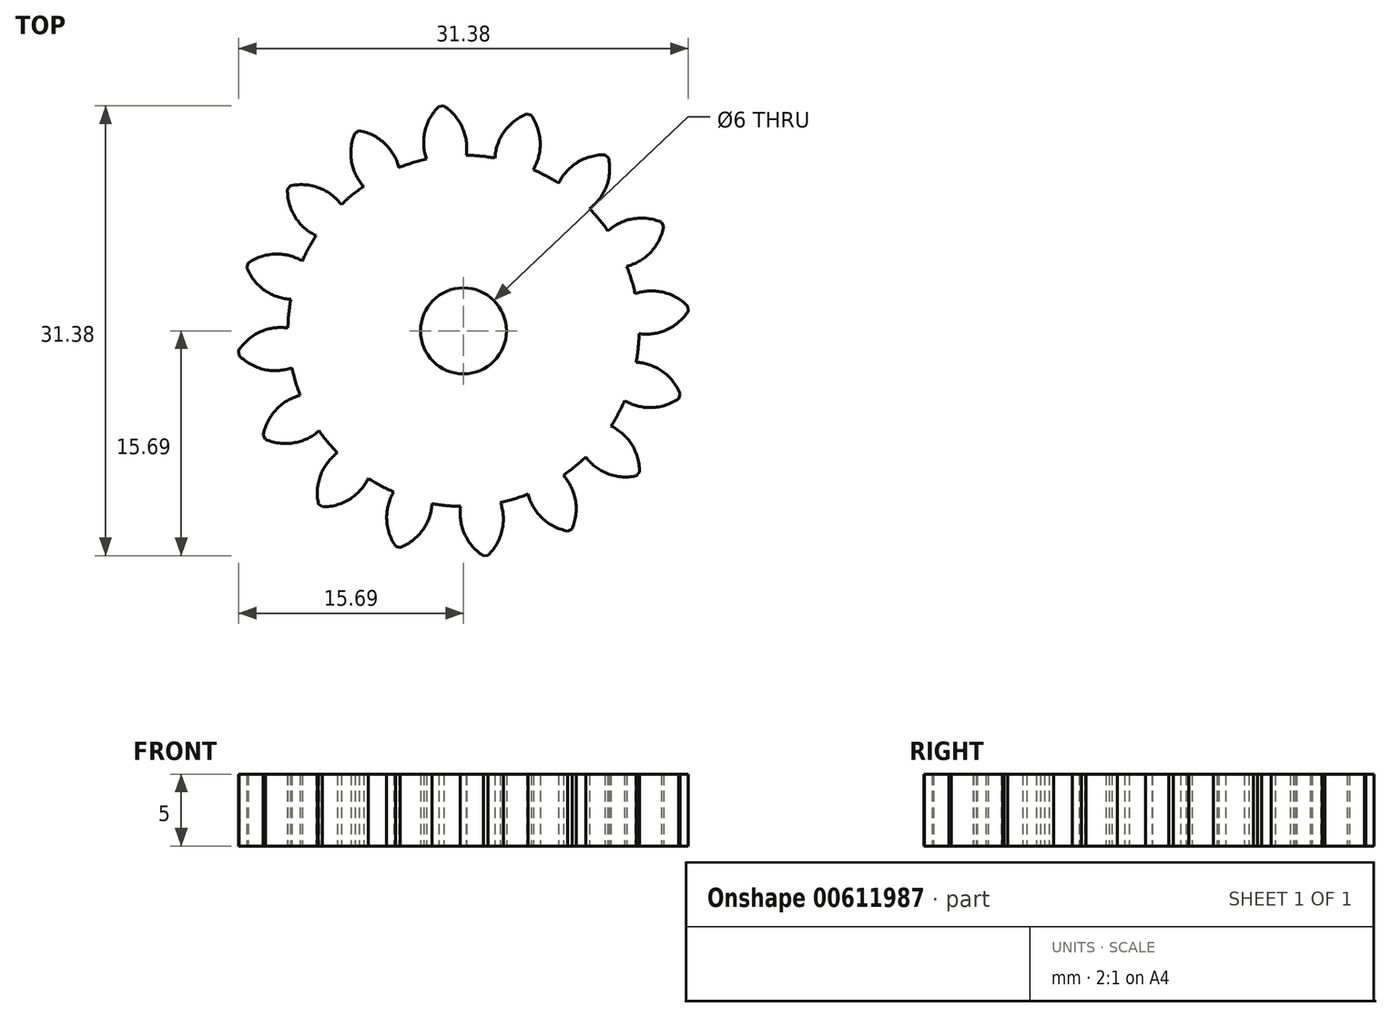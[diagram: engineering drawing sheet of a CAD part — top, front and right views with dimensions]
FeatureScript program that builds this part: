
annotation { "Feature Type Name" : "Feature", "Feature Type Description" : "" }
export const myFeature = defineFeature(function(context is Context, id is Id, definition is map)
    precondition{}
    {
        {
            var Q0;
            Q0=qCreatedBy(makeId("Top.planeOp"),FACE);
            var sketch = newSketch(context, id + "F0", { "sketchPlane" : qUnion([Q0])});
            skCircle(sketch, "E0", {"center": v(0, 0) * mm, "radius": 12.25 * mm});
            skCircle(sketch, "E1", {"center": v(0, 0) * mm, "radius": 14 * mm, "construction": true});
            skCircle(sketch, "E2", {"center": v(0, 0) * mm, "radius": 15.75 * mm, "construction": true});
            skLineSegment(sketch, "E3", {"start": v(0, 0) * mm, "end": v(0, 25.23) * mm, "construction": true});
            skLineSegment(sketch, "E4", {"start": v(0, 0) * mm, "end": v(-2.42, 24.56) * mm, "construction": true});
            skLineSegment(sketch, "E5", {"start": v(0, 14) * mm, "end": v(-23.42, 14) * mm, "construction": true});
            skLineSegment(sketch, "E6", {"start": v(0, 14) * mm, "end": v(-21.75, 6.08) * mm, "construction": true});
            skCircle(sketch, "E7", {"center": v(0, 14) * mm, "radius": 3.5 * mm, "construction": true});
            skCircle(sketch, "E8", {"center": v(0, 0) * mm, "radius": 13.16 * mm, "construction": true});
            skCircle(sketch, "E9", {"center": v(-3.27, 12.74) * mm, "radius": 3.5 * mm, "construction": true});
            skArc(sketch, "E10", {"start": v(0, 14) * mm, "mid": v(-0.56, 14.95) * mm, "end": v(-1.38, 15.69) * mm});
            skArc(sketch, "E11", {"start": v(0.2, 12.25) * mm, "mid": v(0.2, 13.14) * mm, "end": v(0, 14) * mm});
            skArc(sketch, "E12.MirrorCS", {"start": v(-2.73, 13.73) * mm, "mid": v(-2.37, 14.77) * mm, "end": v(-1.71, 15.66) * mm});
            skArc(sketch, "E13.MirrorCS", {"start": v(-2.58, 11.97) * mm, "mid": v(-2.77, 12.84) * mm, "end": v(-2.73, 13.73) * mm});
            skLineSegment(sketch, "E14", {"start": v(-1.71, 15.66) * mm, "end": v(-1.38, 15.69) * mm});
            skSolve(sketch);
        }
        {
            var Q0;
            {var subQ0=sQuery(id+"F0.wireOp",EDGE,"E0");var subQ1=makeQuery(id+"F0.imprint","INTERSECT",VERTEX,{"derivedFrom":[subQ0,sQuery(id+"F0.wireOp",EDGE,"E11")]});Q0=makeQuery(id+"F0.imprint","IMPRINT",FACE,{"disambiguationData":[TD([[makeQuery(id+"F0.imprint","IMPRINT",EDGE,{"disambiguationData":[TD([[subQ1,-1.0]])],"derivedFrom":subQ0}),1.0]])]});}
            extrude(context, id + "F1", {"entities" : qUnion([Q0]), "depth" : 5 * mm, "offsetDistance" : 25 * mm});
        }
        {
            var Q0;
            Q0=makeQuery(id+"F0.imprint","IMPRINT",FACE,{"disambiguationData":[TD([[makeQuery(id+"F0.imprint","IMPRINT",EDGE,{"derivedFrom":sQuery(id+"F0.wireOp",EDGE,"E10")}),1.0]])]});
            extrude(context, id + "F2", {"entities" : qUnion([Q0]), "depth" : 5 * mm, "offsetDistance" : 25 * mm});
        }
        {
            var Q0;
            Q0=makeQuery(id+"F2.opExtrude","SWEPT_BODY",BODY,{"disambiguationData":[OSD([sQuery(id+"F0.wireOp",EDGE,"E0"),sQuery(id+"F0.wireOp",EDGE,"E10"),sQuery(id+"F0.wireOp",EDGE,"E11"),sQuery(id+"F0.wireOp",EDGE,"E12.MirrorCS"),sQuery(id+"F0.wireOp",EDGE,"E13.MirrorCS"),sQuery(id+"F0.wireOp",EDGE,"E14")])]});
            var Q1;
            Q1=makeQuery(id+"F1.opExtrude","CAP_EDGE",EDGE,{"disambiguationData":[OSD([sQuery(id+"F0.wireOp",EDGE,"E0")])],"isStart":false});
            circularPattern(context, id + "F3", {"operationType" : NewBodyOperationType.ADD, "entities" : qUnion([Q0]), "axis" : qUnion([Q1]), "angle" : 360 * degree, "instanceCount" : 16, "equalSpace" : true});
        }
        {
            var Q0;
            Q0=qCreatedBy(makeId("Top.planeOp"),FACE);
            var sketch = newSketch(context, id + "F4", { "sketchPlane" : qUnion([Q0])});
            skLineSegment(sketch, "E15.bottom", {"start": v(6, -16) * mm, "end": v(-6, -16) * mm});
            skLineSegment(sketch, "E15.top", {"start": v(6, 16) * mm, "end": v(-6, 16) * mm});
            skLineSegment(sketch, "E15.left", {"start": v(6, -16) * mm, "end": v(6, 16) * mm});
            skLineSegment(sketch, "E15.right", {"start": v(-6, -16) * mm, "end": v(-6, 16) * mm});
            skPoint(sketch, "E15.middle", {"position": v(0, 0) * mm});
            skCircle(sketch, "E16", {"center": v(0, 16) * mm, "radius": 6 * mm});
            skCircle(sketch, "E17", {"center": v(0, -16) * mm, "radius": 6 * mm});
            skLineSegment(sketch, "E18.bottom", {"start": v(15, -6) * mm, "end": v(-15, -6) * mm});
            skLineSegment(sketch, "E18.top", {"start": v(15, 6) * mm, "end": v(-15, 6) * mm});
            skLineSegment(sketch, "E18.left", {"start": v(15, -6) * mm, "end": v(15, 6) * mm});
            skLineSegment(sketch, "E18.right", {"start": v(-15, -6) * mm, "end": v(-15, 6) * mm});
            skCircle(sketch, "E19", {"center": v(15, 0) * mm, "radius": 6 * mm});
            skCircle(sketch, "E20", {"center": v(-15, 0) * mm, "radius": 6 * mm});
            skSolve(sketch);
        }
        {
            var Q0;
            Q0=sQuery(id+"F4.wireOp",VERTEX,"E15.middle");
            var Q1;
            Q1=makeQuery(id+"F1.opExtrude","SWEPT_BODY",BODY,{"disambiguationData":[OSD([sQuery(id+"F0.wireOp",EDGE,"E0")])]});
            hole(context, id + "F5", {"style" : HoleStyle.SIMPLE, "endStyle" : HoleEndStyle.THROUGH, "oppositeDirection" : true, "holeDiameter" : 6 * mm, "majorDiameter" : 5 * mm, "isTappedThrough" : true, "tappedDepth" : 12 * mm, "tapClearance" : 3, "locations" : qUnion([Q0]), "scope" : qUnion([Q1])});
        }
    });
